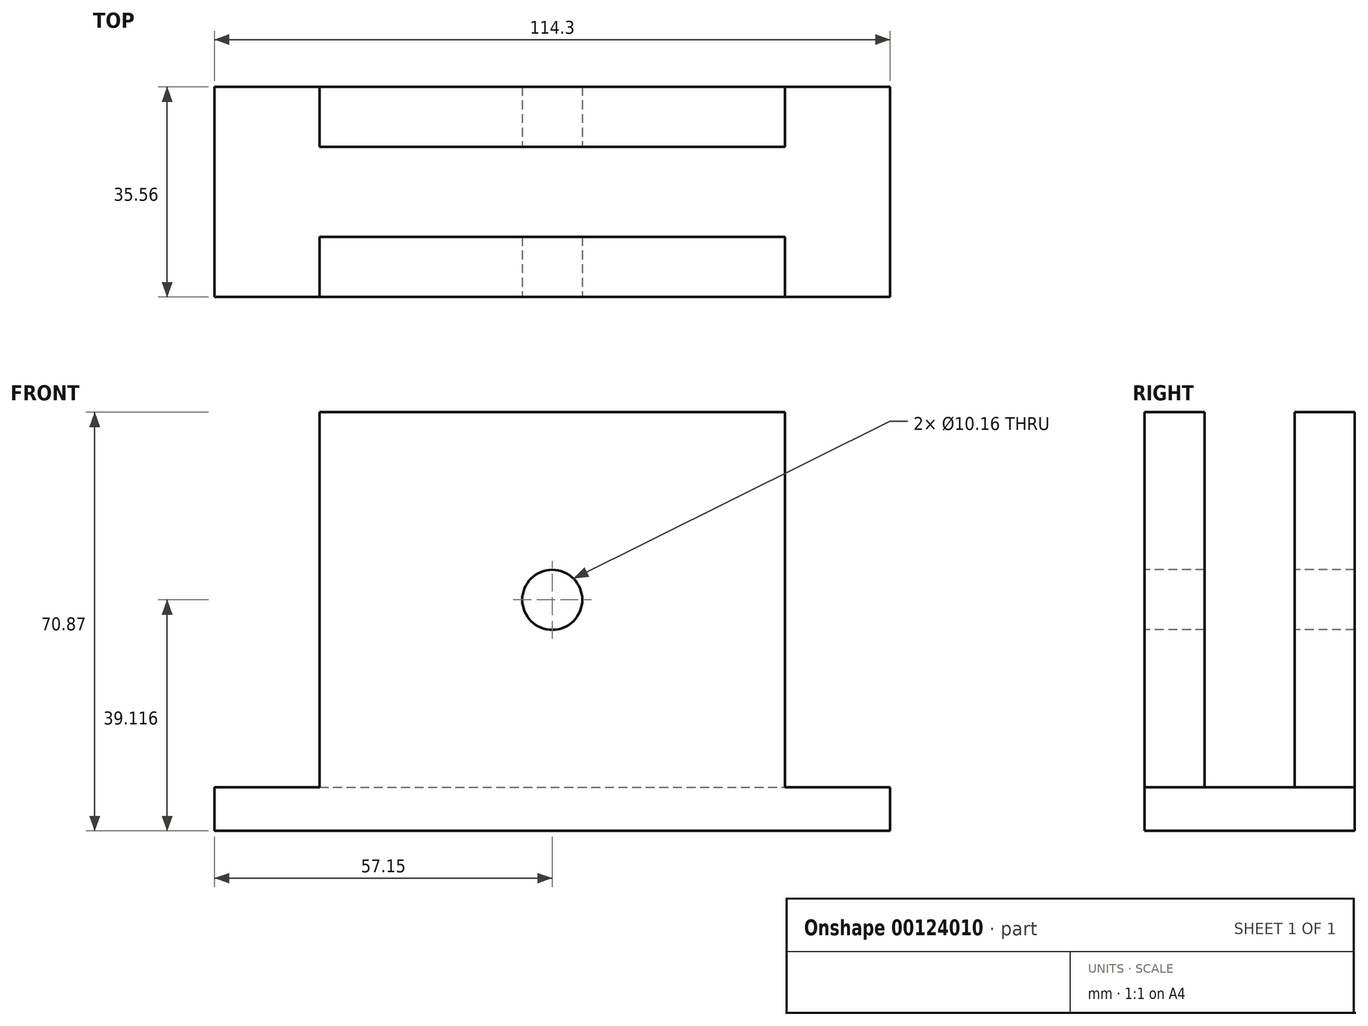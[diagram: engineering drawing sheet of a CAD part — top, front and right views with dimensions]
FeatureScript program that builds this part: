
annotation { "Feature Type Name" : "Feature", "Feature Type Description" : "" }
export const myFeature = defineFeature(function(context is Context, id is Id, definition is map)
    precondition{}
    {
        {
            var Q0;
            Q0=qCreatedBy(makeId("Front.planeOp"),FACE);
            var sketch = newSketch(context, id + "F0", { "sketchPlane" : qUnion([Q0])});
            skLineSegment(sketch, "E0", {"start": v(-57.15, 0) * mm, "end": v(57.15, 0) * mm});
            skPoint(sketch, "E1", {"position": v(0, 0) * mm});
            skLineSegment(sketch, "E2", {"start": v(-57.15, 0) * mm, "end": v(-57.15, 7.37) * mm});
            skLineSegment(sketch, "E3", {"start": v(-57.15, 7.37) * mm, "end": v(57.15, 7.37) * mm});
            skLineSegment(sketch, "E4", {"start": v(57.15, 7.37) * mm, "end": v(57.15, 0) * mm});
            skLineSegment(sketch, "E5", {"start": v(-39.37, 7.37) * mm, "end": v(-39.37, 70.87) * mm});
            skLineSegment(sketch, "E6", {"start": v(-39.37, 70.87) * mm, "end": v(39.37, 70.87) * mm});
            skLineSegment(sketch, "E7", {"start": v(39.37, 70.87) * mm, "end": v(39.37, 7.37) * mm});
            skLineSegment(sketch, "E8", {"start": v(-39.37, 7.37) * mm, "end": v(-57.15, 7.37) * mm});
            skLineSegment(sketch, "E9", {"start": v(57.15, 7.37) * mm, "end": v(39.37, 7.37) * mm});
            skSolve(sketch);
        }
        {
            var Q0;
            Q0 = qSketchRegion(id + "F0", true);
            extrude(context, id + "F1", {"entities" : qUnion([Q0]), "depth" : 35.56 * mm});
        }
        {
            var Q0;
            Q0=makeQuery(id+"F1.opExtrude","SWEPT_FACE",FACE,{"disambiguationData":[OSD([sQuery(id+"F0.wireOp",EDGE,"E7")])]});
            var sketch = newSketch(context, id + "F2", { "sketchPlane" : qUnion([Q0])});
            skLineSegment(sketch, "E10", {"start": v(-25.4, 7.37) * mm, "end": v(-25.4, 70.87) * mm});
            skLineSegment(sketch, "E11", {"start": v(-10.16, 70.87) * mm, "end": v(-10.16, 7.37) * mm});
            skPoint(sketch, "E12", {"position": v(-35.56, 70.87) * mm});
            skPoint(sketch, "E13", {"position": v(0, 70.87) * mm});
            skLineSegment(sketch, "E14", {"start": v(-25.4, 70.87) * mm, "end": v(-10.16, 70.87) * mm});
            skLineSegment(sketch, "E15", {"start": v(-10.16, 7.37) * mm, "end": v(-25.4, 7.37) * mm});
            skSolve(sketch);
        }
        {
            var Q0;
            Q0 = qSketchRegion(id + "F2", true);
            extrude(context, id + "F3", {"entities" : qUnion([Q0]), "operationType" : NewBodyOperationType.REMOVE, "oppositeDirection" : true, "depth" : 127 * mm});
        }
        {
            var Q0;
            Q0=makeQuery(id+"F1.opExtrude","CAP_FACE",FACE,{"disambiguationData":[OSD([sQuery(id+"F0.wireOp",EDGE,"E0"),sQuery(id+"F0.wireOp",EDGE,"E2"),sQuery(id+"F0.wireOp",EDGE,"E4"),sQuery(id+"F0.wireOp",EDGE,"E5"),sQuery(id+"F0.wireOp",EDGE,"E6"),sQuery(id+"F0.wireOp",EDGE,"E7"),sQuery(id+"F0.wireOp",EDGE,"E8"),sQuery(id+"F0.wireOp",EDGE,"E9")])],"isStart":false});
            var sketch = newSketch(context, id + "F4", { "sketchPlane" : qUnion([Q0])});
            skLineSegment(sketch, "E16", {"start": v(0, 0) * mm, "end": v(0, 70.87) * mm, "construction": true});
            skLineSegment(sketch, "E17", {"start": v(-39.37, 39.12) * mm, "end": v(39.37, 39.12) * mm, "construction": true});
            skPoint(sketch, "E18", {"position": v(0, 39.12) * mm});
            skCircle(sketch, "E19", {"center": v(0, 39.12) * mm, "radius": 5.08 * mm});
            skSolve(sketch);
        }
        {
            var Q0;
            Q0 = qSketchRegion(id + "F4", true);
            extrude(context, id + "F5", {"entities" : qUnion([Q0]), "operationType" : NewBodyOperationType.REMOVE, "oppositeDirection" : true, "depth" : 76.2 * mm});
        }
    });
